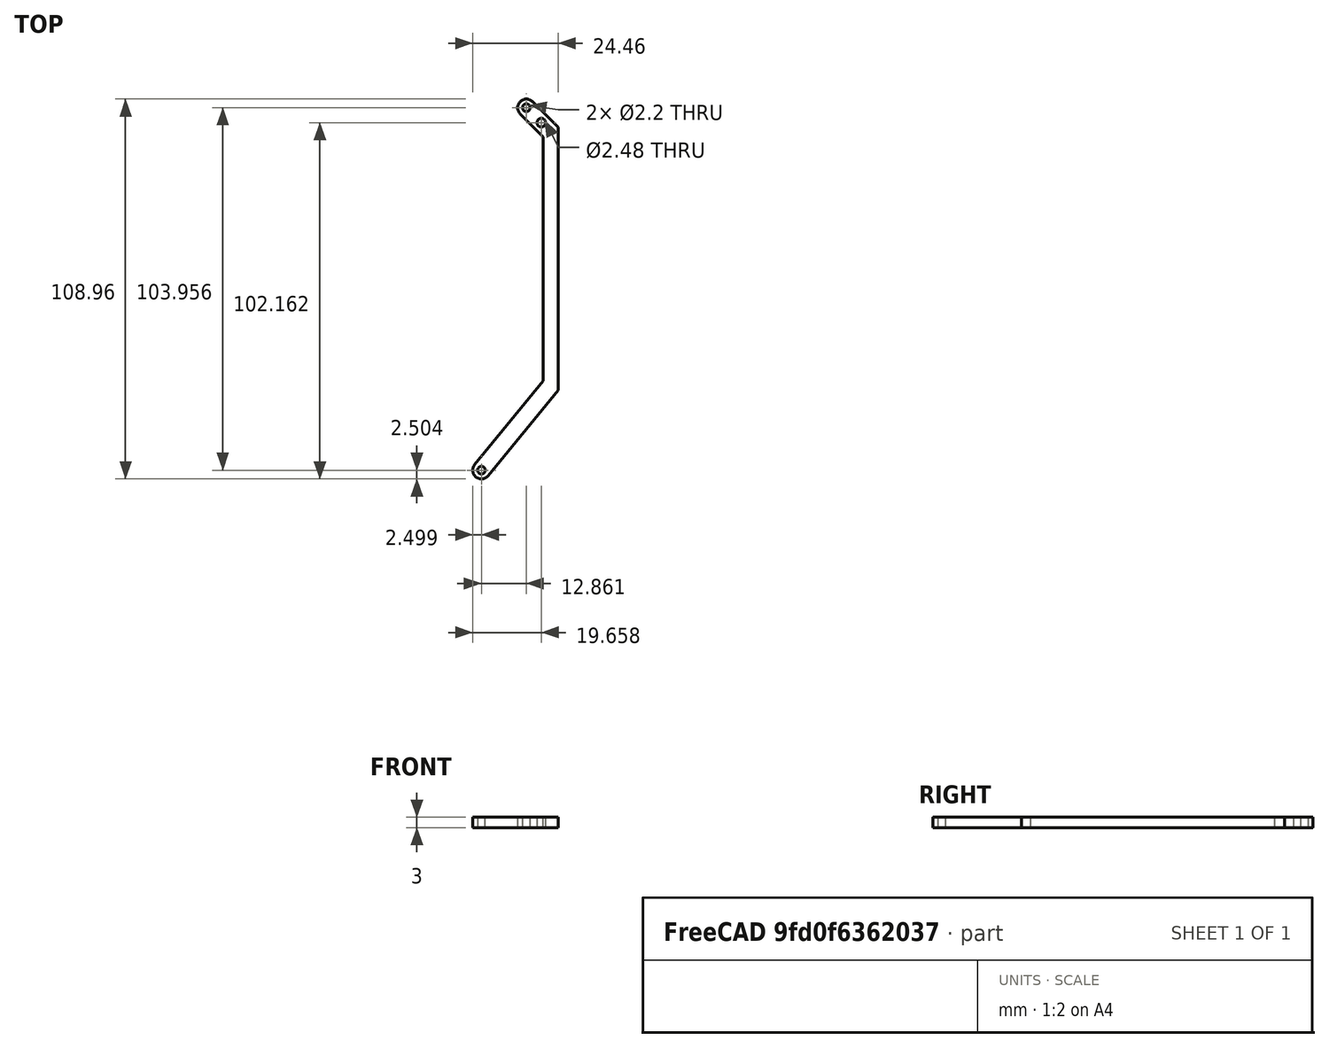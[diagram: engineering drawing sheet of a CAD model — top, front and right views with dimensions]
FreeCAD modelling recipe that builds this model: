
FCSTD DOCUMENT  (FreeCAD 0.20R29603 (Git))
Label: RearLinkage
License: All rights reserved
LicenseURL: http://en.wikipedia.org/wiki/All_rights_reserved
objects: PartDesign::CoordinateSystem×4, Sketcher::SketchObject×1, PartDesign::Pad×1, PartDesign::Body×1
note: 8 computed .brp shape members not serialized (recipe doc carries the construction recipe); baked Part::Feature solids carry a one-line shape summary decoded from their .brp

FEATURE [PartDesign::CoordinateSystem] LCS_0  label="center_lcs"
  AttacherType = Attacher::AttachEngine3D
  MapMode = 2
  Support = -> [X_Axis]
FEATURE [Sketcher::SketchObject] Sketch_1  label="bar_sketch"
  FullyConstrained = false
  sketch-geometry (12):
    g0: Circle CenterX=-12.8608 CenterY=-103.956 CenterZ=0 NormalX=0 NormalY=0 NormalZ=1 AngleXU=0 Radius=1.1
    g1: ArcOfCircle CenterX=0 CenterY=0 CenterZ=0 NormalX=0 NormalY=0 NormalZ=1 AngleXU=0 Radius=2.5 StartAngle=0.785398 EndAngle=3.92699
    g2: ArcOfCircle CenterX=-12.8608 CenterY=-103.956 CenterZ=0 NormalX=0 NormalY=0 NormalZ=1 AngleXU=0 Radius=2.5 StartAngle=2.45611 EndAngle=5.59771
    g3: Circle CenterX=0 CenterY=0 CenterZ=0 NormalX=0 NormalY=0 NormalZ=1 AngleXU=0 Radius=1.1
    g4: LineSegment StartX=-1.76777 StartY=-1.76777 StartZ=0 EndX=4.83621 EndY=-8.37175 EndZ=0
    g5: LineSegment StartX=1.76777 StartY=1.76777 StartZ=0 EndX=9.09799 EndY=-5.56246 EndZ=0
    g6: Circle CenterX=4.29775 CenterY=-4.29775 CenterZ=0 NormalX=0 NormalY=0 NormalZ=1 AngleXU=0 Radius=1.24062
    g7: LineSegment StartX=0 StartY=0 StartZ=0 EndX=4.29775 EndY=-4.29775 EndZ=0
    g8: LineSegment StartX=9.09799 StartY=-5.56246 StartZ=0 EndX=9.09799 EndY=-81.0529 EndZ=0
    g9: LineSegment StartX=4.83621 StartY=-8.37175 StartZ=0 EndX=4.83621 EndY=-78.366 EndZ=0
    g10: LineSegment StartX=9.09799 StartY=-81.0529 StartZ=0 EndX=-10.9255 EndY=-105.539 EndZ=0
    g11: LineSegment StartX=4.83621 StartY=-78.366 StartZ=0 EndX=-14.7961 EndY=-102.373 EndZ=0
  constraints (23):
    c: Diameter(g0) = 2.2
    c: Distance(g1,g1) = 5
    c: Coincident(g2,g0)
    c: Coincident(g3,g1)
    c: Equal(g3,g0)
    c: Parallel(g5,g4)
    c: Tangent(g5,g1) = 1.5708
    c: Tangent(g4,g1) = -1.5708
    c: Equal(g1,g2)
    c: Coincident(g7,g1)
    c: Coincident(g7,g6)
    c: Parallel(g5,g7)
    c: Angle(g5) = -0.785398
    c: Coincident(g-1,g1)
    c: Coincident(g8,g5)
    c: Vertical(g8)
    c: Coincident(g9,g4)
    c: Vertical(g9)
    c: Coincident(g10,g8)
    c: Coincident(g11,g9)
    c: Parallel(g10,g11)
    c: Tangent(g11,g2) = -1.5708
    c: Tangent(g10,g2) = 1.5708
FEATURE [PartDesign::Pad] Pad  label="bar_pad"
  Direction = (0,0,1)
  Length = 3
  Length2 = 10
  Profile = -> Sketch_1
  ReferenceAxis = -> Sketch_1 [N_Axis]
  Type = 0
FEATURE [PartDesign::CoordinateSystem] LCS_1  label="hole_1_lcs"
  AttacherType = Attacher::AttachEngine3D
  MapMode = 11
  Placement = pos=(0,0,3) rot=(0,0,1;1.5708rad)
  Support = -> [Pad]
FEATURE [PartDesign::CoordinateSystem] hole_2  label="hole_2_lcs"
  AttacherType = Attacher::AttachEngine3D
  MapMode = 11
  Placement = pos=(4.29775,-4.29775,3) rot=(0,0,1;1.5708rad)
  Support = -> [Pad]
FEATURE [PartDesign::CoordinateSystem] hole_3_lcs
  AttacherType = Attacher::AttachEngine3D
  MapMode = 11
  Placement = pos=(-12.8608,-103.956,3) rot=(0,0,1;1.5708rad)
  Support = -> [Pad]
FEATURE [PartDesign::Body] rear_linkage_body
  Group = -> [LCS_0,Sketch_1,Pad,LCS_1,hole_2,hole_3_lcs]
  Origin = -> Origin
  Tip = -> Pad
